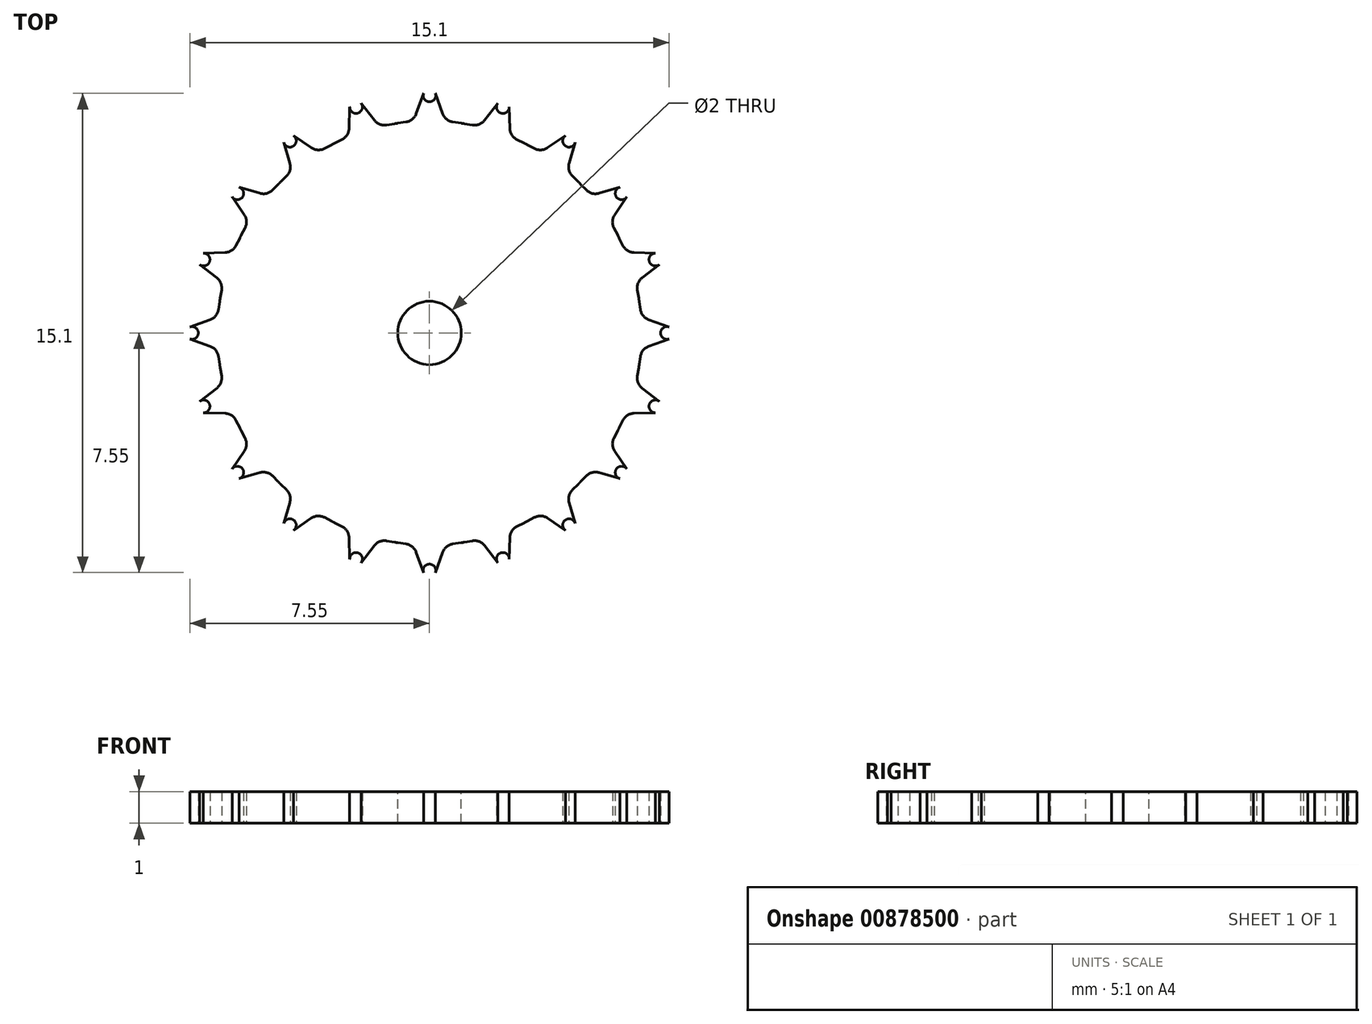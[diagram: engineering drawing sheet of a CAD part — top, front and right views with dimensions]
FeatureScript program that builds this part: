
annotation { "Feature Type Name" : "Feature", "Feature Type Description" : "" }
export const myFeature = defineFeature(function(context is Context, id is Id, definition is map)
    precondition{}
    {
        {
            var Q0;
            Q0=qCreatedBy(makeId("Top.planeOp"),FACE);
            var sketch = newSketch(context, id + "F0", { "sketchPlane" : qUnion([Q0])});
            skCircle(sketch, "E0", {"center": v(0, 0) * mm, "radius": 6.68 * mm});
            skLineSegment(sketch, "E1", {"start": v(0, 6.68) * mm, "end": v(0, 7.68) * mm});
            skLineSegment(sketch, "E2", {"start": v(0, 6.68) * mm, "end": v(0.5, 6.68) * mm});
            skLineSegment(sketch, "E3", {"start": v(0, 6.68) * mm, "end": v(-0.5, 6.68) * mm});
            skCircle(sketch, "E4", {"center": v(0, 7.49) * mm, "radius": 0.2 * mm});
            skLineSegment(sketch, "E5", {"start": v(0.42, 6.9) * mm, "end": v(0.19, 7.55) * mm});
            skLineSegment(sketch, "E6", {"start": v(-0.19, 7.55) * mm, "end": v(-0.42, 6.9) * mm});
            skLineSegment(sketch, "E7", {"start": v(-0.74, 6.65) * mm, "end": v(-1, 6.61) * mm});
            skLineSegment(sketch, "E8", {"start": v(0.74, 6.65) * mm, "end": v(1, 6.61) * mm});
            skPoint(sketch, "E9.visualSharp", {"position": v(-0.5, 6.68) * mm});
            skArc(sketch, "E9.filletArc", {"start": v(-0.74, 6.65) * mm, "mid": v(-0.54, 6.74) * mm, "end": v(-0.42, 6.9) * mm});
            skPoint(sketch, "E10.visualSharp", {"position": v(0.5, 6.68) * mm});
            skArc(sketch, "E10.filletArc", {"start": v(0.42, 6.9) * mm, "mid": v(0.54, 6.74) * mm, "end": v(0.74, 6.65) * mm});
            skSolve(sketch);
        }
        {
            var Q0;
            {var subQ0=sQuery(id+"F0.wireOp",EDGE,"E4");var subQ1=sQuery(id+"F0.wireOp",EDGE,"E1");var subQ2=makeQuery(id+"F0.imprint","INTERSECT",VERTEX,{"disambiguationData":[OD(0.0)],"derivedFrom":[subQ1,subQ0]});Q0=makeQuery(id+"F0.imprint","IMPRINT",FACE,{"disambiguationData":[TD([[makeQuery(id+"F0.imprint","IMPRINT",EDGE,{"disambiguationData":[TD([[subQ2,1.0]])],"derivedFrom":subQ1}),-1.0]])]});}
            var Q1;
            {var subQ0=sQuery(id+"F0.wireOp",EDGE,"E4");var subQ1=sQuery(id+"F0.wireOp",EDGE,"E1");var subQ2=makeQuery(id+"F0.imprint","INTERSECT",VERTEX,{"disambiguationData":[OD(0.0)],"derivedFrom":[subQ1,subQ0]});Q1=makeQuery(id+"F0.imprint","IMPRINT",FACE,{"disambiguationData":[TD([[makeQuery(id+"F0.imprint","IMPRINT",EDGE,{"disambiguationData":[TD([[subQ2,1.0]])],"derivedFrom":subQ1}),1.0]])]});}
            var Q2;
            {var subQ0=sQuery(id+"F0.wireOp",EDGE,"E6");Q2=makeQuery(id+"F0.imprint","IMPRINT",FACE,{"disambiguationData":[TD([[makeQuery(id+"F0.imprint","IMPRINT",EDGE,{"derivedFrom":subQ0}),1.0]])]});}
            var Q3;
            {var subQ0=sQuery(id+"F0.wireOp",EDGE,"E5");Q3=makeQuery(id+"F0.imprint","IMPRINT",FACE,{"disambiguationData":[TD([[makeQuery(id+"F0.imprint","IMPRINT",EDGE,{"derivedFrom":subQ0}),1.0]])]});}
            var Q4;
            {var subQ0=sQuery(id+"F0.wireOp",EDGE,"E0");var subQ1=makeQuery(id+"F0.imprint","INTERSECT",VERTEX,{"derivedFrom":[subQ0,sQuery(id+"F0.wireOp",EDGE,"E1")]});Q4=makeQuery(id+"F0.imprint","IMPRINT",FACE,{"disambiguationData":[TD([[makeQuery(id+"F0.imprint","IMPRINT",EDGE,{"disambiguationData":[TD([[subQ1,1.0]])],"derivedFrom":subQ0}),1.0]])]});}
            extrude(context, id + "F1", {"entities" : qUnion([Q0, Q1, Q2, Q3, Q4]), "depth" : 1 * mm, "offsetDistance" : 25 * mm});
        }
        {
            var Q0;
            Q0=makeQuery(id+"F1.opExtrude","SWEPT_BODY",BODY,{"disambiguationData":[OSD([sQuery(id+"F0.wireOp",EDGE,"E0"),sQuery(id+"F0.wireOp",EDGE,"E4"),sQuery(id+"F0.wireOp",EDGE,"E5"),sQuery(id+"F0.wireOp",EDGE,"E6"),sQuery(id+"F0.wireOp",EDGE,"E7"),sQuery(id+"F0.wireOp",EDGE,"E8"),sQuery(id+"F0.wireOp",EDGE,"E9.filletArc"),sQuery(id+"F0.wireOp",EDGE,"E10.filletArc")])]});
            var Q1;
            Q1=makeQuery(id+"F1.opExtrude","SWEPT_FACE",FACE,{"disambiguationData":[OSD([sQuery(id+"F0.wireOp",EDGE,"E8")])]});
            var Q2;
            Q2=makeQuery(id+"F1.opExtrude","SWEPT_FACE",FACE,{"disambiguationData":[OSD([sQuery(id+"F0.wireOp",EDGE,"E10.filletArc")])]});
            var Q3;
            Q3=makeQuery(id+"F1.opExtrude","SWEPT_FACE",FACE,{"disambiguationData":[OSD([sQuery(id+"F0.wireOp",EDGE,"E5")])]});
            var Q4;
            Q4=makeQuery(id+"F1.opExtrude","SWEPT_FACE",FACE,{"disambiguationData":[OSD([sQuery(id+"F0.wireOp",EDGE,"E4")])]});
            var Q5;
            Q5=makeQuery(id+"F1.opExtrude","SWEPT_FACE",FACE,{"disambiguationData":[OSD([sQuery(id+"F0.wireOp",EDGE,"E6")])]});
            var Q6;
            Q6=makeQuery(id+"F1.opExtrude","SWEPT_FACE",FACE,{"disambiguationData":[OSD([sQuery(id+"F0.wireOp",EDGE,"E9.filletArc")])]});
            var Q7;
            Q7=makeQuery(id+"F1.opExtrude","SWEPT_FACE",FACE,{"disambiguationData":[OSD([sQuery(id+"F0.wireOp",EDGE,"E7")])]});
            var Q8;
            Q8=makeQuery(id+"F1.opExtrude","SWEPT_FACE",FACE,{"disambiguationData":[OSD([sQuery(id+"F0.wireOp",EDGE,"E0")])]});
            circularPattern(context, id + "F2", {"patternType" : PatternType.FACE, "faces" : qUnion([Q1, Q2, Q3, Q4, Q5, Q6, Q7]), "axis" : qUnion([Q8]), "angle" : 360 * degree, "instanceCount" : 60, "equalSpace" : true});
        }
        {
            var Q0;
            Q0=makeQuery(id+"F1.opExtrude","CAP_FACE",FACE,{"disambiguationData":[OSD([sQuery(id+"F0.wireOp",EDGE,"E0"),sQuery(id+"F0.wireOp",EDGE,"E4"),sQuery(id+"F0.wireOp",EDGE,"E5"),sQuery(id+"F0.wireOp",EDGE,"E6"),sQuery(id+"F0.wireOp",EDGE,"E7"),sQuery(id+"F0.wireOp",EDGE,"E8"),sQuery(id+"F0.wireOp",EDGE,"E9.filletArc"),sQuery(id+"F0.wireOp",EDGE,"E10.filletArc")])],"isStart":false});
            var sketch = newSketch(context, id + "F3", { "sketchPlane" : qUnion([Q0])});
            skCircle(sketch, "E11", {"center": v(0, 0) * mm, "radius": 1 * mm});
            skSolve(sketch);
        }
        {
            var Q0;
            Q0=makeQuery(id+"F3.imprint","IMPRINT",FACE,{"disambiguationData":[TD([[makeQuery(id+"F3.imprint","IMPRINT",EDGE,{"derivedFrom":sQuery(id+"F3.wireOp",EDGE,"E11")}),1.0]])]});
            extrude(context, id + "F4", {"entities" : qUnion([Q0]), "operationType" : NewBodyOperationType.REMOVE, "endBound" : BoundingType.THROUGH_ALL, "oppositeDirection" : true, "depth" : 25 * mm, "offsetDistance" : 25 * mm});
        }
    });
